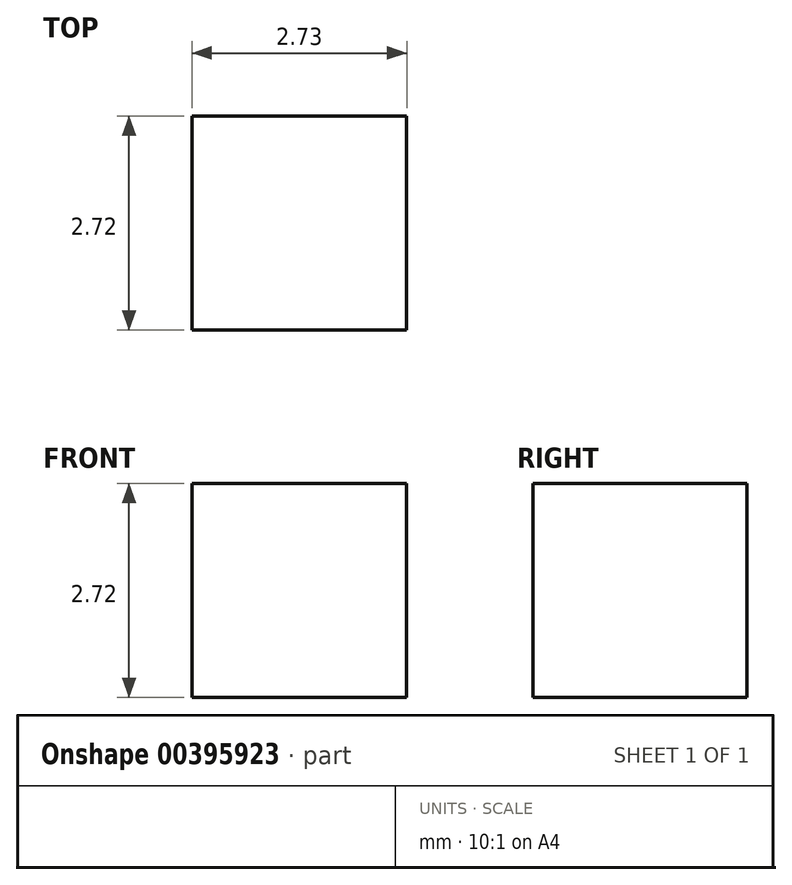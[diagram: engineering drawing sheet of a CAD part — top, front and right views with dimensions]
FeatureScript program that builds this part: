
annotation { "Feature Type Name" : "Feature", "Feature Type Description" : "" }
export const myFeature = defineFeature(function(context is Context, id is Id, definition is map)
    precondition{}
    {
        {
            var Q0;
            Q0=qCreatedBy(makeId("Top.planeOp"),FACE);
            var sketch = newSketch(context, id + "F0", { "sketchPlane" : qUnion([Q0])});
            skLineSegment(sketch, "E0.bottom", {"start": v(0, 0) * mm, "end": v(2.73, 0) * mm});
            skLineSegment(sketch, "E0.top", {"start": v(0, -2.72) * mm, "end": v(2.73, -2.72) * mm});
            skLineSegment(sketch, "E0.left", {"start": v(0, 0) * mm, "end": v(0, -2.72) * mm});
            skLineSegment(sketch, "E0.right", {"start": v(2.73, 0) * mm, "end": v(2.73, -2.72) * mm});
            skSolve(sketch);
        }
        {
            var Q0;
            Q0=makeQuery(id+"F0.imprint","IMPRINT",FACE,{"disambiguationData":[TD([[makeQuery(id+"F0.imprint","IMPRINT",EDGE,{"derivedFrom":sQuery(id+"F0.wireOp",EDGE,"E0.bottom")}),-1.0]])]});
            extrude(context, id + "F1", {"entities" : qUnion([Q0]), "depth" : 2.72 * mm});
        }
    });
